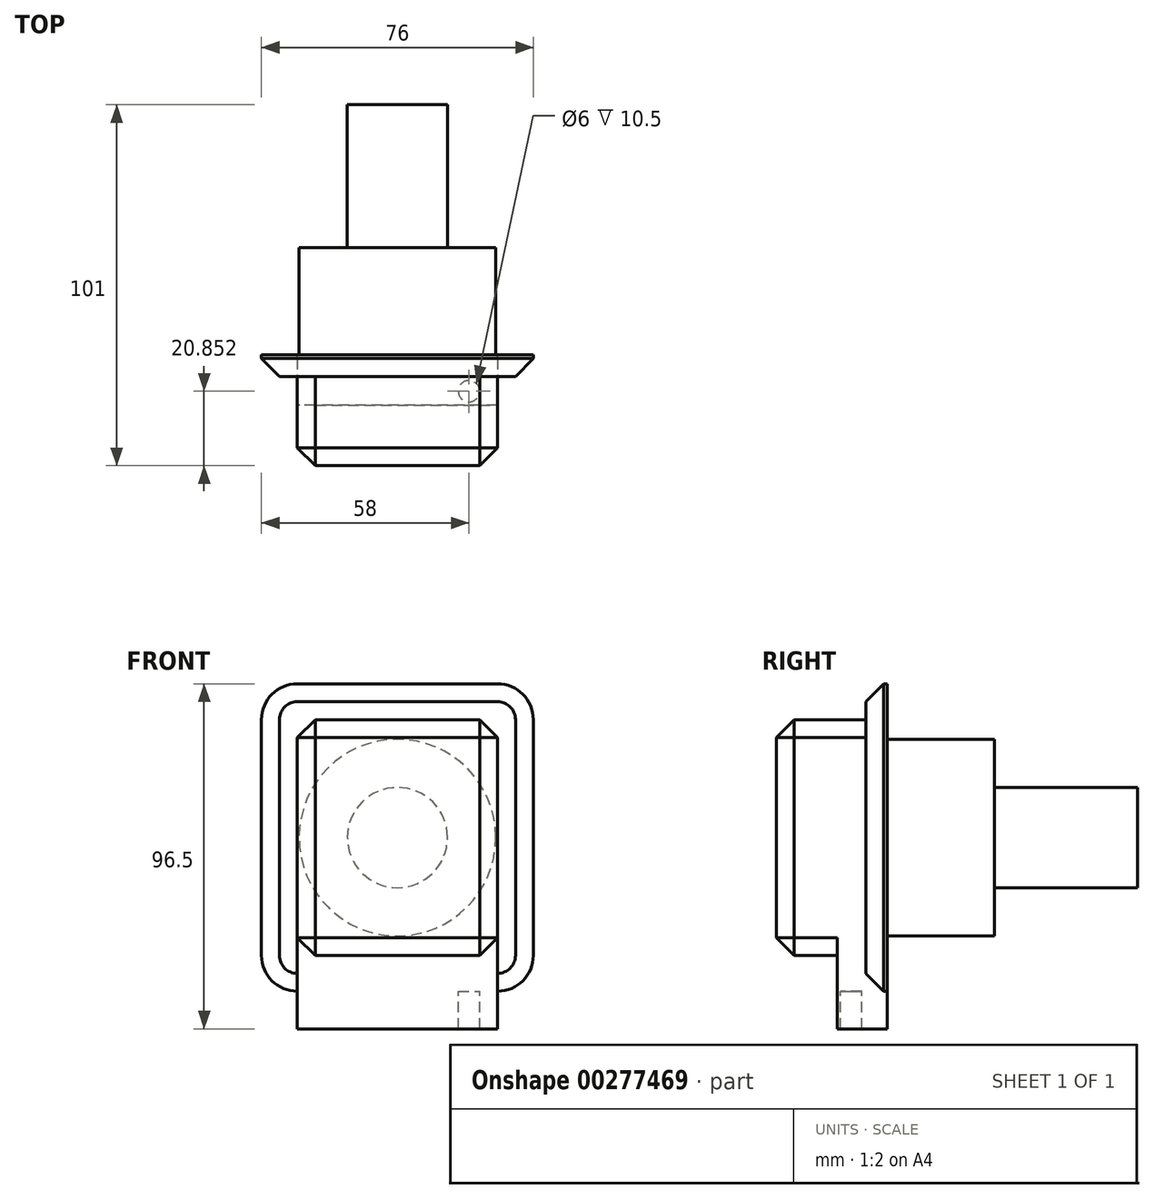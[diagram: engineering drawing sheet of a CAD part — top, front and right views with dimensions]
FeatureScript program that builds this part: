
annotation { "Feature Type Name" : "Feature", "Feature Type Description" : "" }
export const myFeature = defineFeature(function(context is Context, id is Id, definition is map)
    precondition{}
    {
        {
            var Q0;
            Q0=qCreatedBy(makeId("Front.planeOp"),FACE);
            var sketch = newSketch(context, id + "F0", { "sketchPlane" : qUnion([Q0])});
            skLineSegment(sketch, "E0.bottom", {"start": v(28, 43) * mm, "end": v(-28, 43) * mm});
            skLineSegment(sketch, "E0.top", {"start": v(28, -43) * mm, "end": v(-28, -43) * mm});
            skLineSegment(sketch, "E0.left", {"start": v(38, 33) * mm, "end": v(38, -33) * mm});
            skLineSegment(sketch, "E0.right", {"start": v(-38, 33) * mm, "end": v(-38, -33) * mm});
            skPoint(sketch, "E0.middle", {"position": v(0, 0) * mm});
            skPoint(sketch, "E1.visualSharp", {"position": v(-38, 43) * mm});
            skArc(sketch, "E1.filletArc", {"start": v(-28, 43) * mm, "mid": v(-35.07, 40.07) * mm, "end": v(-38, 33) * mm});
            skPoint(sketch, "E2.visualSharp", {"position": v(38, 43) * mm});
            skArc(sketch, "E2.filletArc", {"start": v(38, 33) * mm, "mid": v(35.07, 40.07) * mm, "end": v(28, 43) * mm});
            skPoint(sketch, "E3.visualSharp", {"position": v(38, -43) * mm});
            skArc(sketch, "E3.filletArc", {"start": v(28, -43) * mm, "mid": v(35.07, -40.07) * mm, "end": v(38, -33) * mm});
            skPoint(sketch, "E4.visualSharp", {"position": v(-38, -43) * mm});
            skArc(sketch, "E4.filletArc", {"start": v(-38, -33) * mm, "mid": v(-35.07, -40.07) * mm, "end": v(-28, -43) * mm});
            skSolve(sketch);
        }
        {
            var Q0;
            Q0=qSketchRegion(id+"F0",true);
            extrude(context, id + "F1", {"entities" : qUnion([Q0]), "depth" : 6 * mm});
        }
        {
            var Q0;
            Q0=makeQuery(id+"F1.opExtrude","CAP_FACE",FACE,{"disambiguationData":[OSD([sQuery(id+"F0.wireOp",EDGE,"E0.bottom"),sQuery(id+"F0.wireOp",EDGE,"E0.top"),sQuery(id+"F0.wireOp",EDGE,"E0.left"),sQuery(id+"F0.wireOp",EDGE,"E0.right")])],"isStart":true});
            var sketch = newSketch(context, id + "F2", { "sketchPlane" : qUnion([Q0])});
            skCircle(sketch, "E5", {"center": v(0, 0) * mm, "radius": 27.5 * mm});
            skSolve(sketch);
        }
        {
            var Q0;
            Q0=qSketchRegion(id+"F2",true);
            extrude(context, id + "F3", {"entities" : qUnion([Q0]), "operationType" : NewBodyOperationType.ADD, "depth" : 30 * mm});
        }
        {
            var Q0;
            Q0=makeQuery(id+"F3.opExtrude","CAP_FACE",FACE,{"disambiguationData":[OSD([sQuery(id+"F2.wireOp",EDGE,"E5")])],"isStart":false});
            var sketch = newSketch(context, id + "F4", { "sketchPlane" : qUnion([Q0])});
            skCircle(sketch, "E6", {"center": v(0, 0) * mm, "radius": 14 * mm});
            skSolve(sketch);
        }
        {
            var Q0;
            Q0=makeQuery(id+"F4.imprint","IMPRINT",FACE,{"disambiguationData":[TD([[makeQuery(id+"F4.imprint","IMPRINT",EDGE,{"derivedFrom":sQuery(id+"F4.wireOp",EDGE,"E6")}),1.0]])]});
            extrude(context, id + "F5", {"entities" : qUnion([Q0]), "operationType" : NewBodyOperationType.ADD, "depth" : 40 * mm});
        }
        {
            var Q0;
            Q0=makeQuery(id+"F1.opExtrude","CAP_FACE",FACE,{"disambiguationData":[OSD([sQuery(id+"F0.wireOp",EDGE,"E0.bottom"),sQuery(id+"F0.wireOp",EDGE,"E0.top"),sQuery(id+"F0.wireOp",EDGE,"E0.left"),sQuery(id+"F0.wireOp",EDGE,"E0.right"),sQuery(id+"F0.wireOp",EDGE,"E1.filletArc"),sQuery(id+"F0.wireOp",EDGE,"E2.filletArc"),sQuery(id+"F0.wireOp",EDGE,"E3.filletArc"),sQuery(id+"F0.wireOp",EDGE,"E4.filletArc")])],"isStart":false});
            var sketch = newSketch(context, id + "F6", { "sketchPlane" : qUnion([Q0])});
            skPoint(sketch, "E7.0", {"position": v(-28, -43) * mm});
            skLineSegment(sketch, "E8.bottom", {"start": v(-28, -43) * mm, "end": v(28, -43) * mm});
            skLineSegment(sketch, "E8.top", {"start": v(-28, -33) * mm, "end": v(28, -33) * mm});
            skLineSegment(sketch, "E8.left", {"start": v(-28, -43) * mm, "end": v(-28, -33) * mm});
            skLineSegment(sketch, "E8.right", {"start": v(28, -43) * mm, "end": v(28, -33) * mm});
            skSolve(sketch);
        }
        {
            var Q0;
            Q0=qSketchRegion(id+"F6",true);
            extrude(context, id + "F7", {"entities" : qUnion([Q0]), "operationType" : NewBodyOperationType.ADD, "depth" : 8 * mm});
        }
        {
            var Q0;
            Q0=makeQuery(id+"F7.boolean.opBoolean","MERGE",FACE,{"derivedFrom":[makeQuery(id+"F1.opExtrude","SWEPT_FACE",FACE,{"disambiguationData":[OSD([sQuery(id+"F0.wireOp",EDGE,"E0.top")])]}),makeQuery(id+"F7.opExtrude","SWEPT_FACE",FACE,{"disambiguationData":[OSD([sQuery(id+"F6.wireOp",EDGE,"E8.bottom")])]})]});
            var sketch = newSketch(context, id + "F8", { "sketchPlane" : qUnion([Q0])});
            skCircle(sketch, "E9", {"center": v(-20, 10.15) * mm, "radius": 3 * mm});
            skCircle(sketch, "E10.MirrorC", {"center": v(20, 10.15) * mm, "radius": 3 * mm});
            skSolve(sketch);
        }
        {
            var Q0;
            Q0=makeQuery(id+"F8.imprint","IMPRINT",FACE,{"disambiguationData":[TD([[makeQuery(id+"F8.imprint","IMPRINT",EDGE,{"derivedFrom":sQuery(id+"F8.wireOp",EDGE,"E9")}),1.0]])]});
            var Q1;
            Q1=makeQuery(id+"F8.imprint","IMPRINT",FACE,{"disambiguationData":[TD([[makeQuery(id+"F8.imprint","IMPRINT",EDGE,{"derivedFrom":sQuery(id+"F8.wireOp",EDGE,"E10.MirrorC")}),-1.0]])]});
            extrude(context, id + "F9", {"entities" : qUnion([Q0, Q1]), "operationType" : NewBodyOperationType.ADD, "depth" : 10.5 * mm});
        }
        {
            var Q0;
            Q0=makeQuery(id+"F1.opExtrude","CAP_FACE",FACE,{"disambiguationData":[OSD([sQuery(id+"F0.wireOp",EDGE,"E0.bottom"),sQuery(id+"F0.wireOp",EDGE,"E0.top"),sQuery(id+"F0.wireOp",EDGE,"E0.left"),sQuery(id+"F0.wireOp",EDGE,"E0.right"),sQuery(id+"F0.wireOp",EDGE,"E1.filletArc"),sQuery(id+"F0.wireOp",EDGE,"E2.filletArc"),sQuery(id+"F0.wireOp",EDGE,"E3.filletArc"),sQuery(id+"F0.wireOp",EDGE,"E4.filletArc")])],"isStart":false});
            var sketch = newSketch(context, id + "F10", { "sketchPlane" : qUnion([Q0])});
            skLineSegment(sketch, "E11.bottom", {"start": v(-28, 33) * mm, "end": v(28, 33) * mm});
            skLineSegment(sketch, "E11.top", {"start": v(-28, -33) * mm, "end": v(28, -33) * mm});
            skLineSegment(sketch, "E11.left", {"start": v(-28, 33) * mm, "end": v(-28, -33) * mm});
            skLineSegment(sketch, "E11.right", {"start": v(28, 33) * mm, "end": v(28, -33) * mm});
            skSolve(sketch);
        }
        {
            var Q0;
            Q0=qSketchRegion(id+"F10",true);
            extrude(context, id + "F11", {"entities" : qUnion([Q0]), "operationType" : NewBodyOperationType.ADD, "depth" : 25 * mm});
        }
        {
            var Q0;
            Q0=makeQuery(id+"F11.opExtrude","CAP_EDGE",EDGE,{"disambiguationData":[OSD([sQuery(id+"F10.wireOp",EDGE,"E11.bottom")])],"isStart":false});
            var Q1;
            Q1=makeQuery(id+"F11.opExtrude","CAP_EDGE",EDGE,{"disambiguationData":[OSD([sQuery(id+"F10.wireOp",EDGE,"E11.right")])],"isStart":false});
            var Q2;
            Q2=makeQuery(id+"F11.opExtrude","CAP_EDGE",EDGE,{"disambiguationData":[OSD([sQuery(id+"F10.wireOp",EDGE,"E11.left")])],"isStart":false});
            var Q3;
            Q3=makeQuery(id+"F11.opExtrude","SWEPT_EDGE",EDGE,{"disambiguationData":[OSD([sQuery(id+"F10.wireOp",EDGE,"E11.bottom"),sQuery(id+"F10.wireOp",EDGE,"E11.left")])]});
            var Q4;
            Q4=makeQuery(id+"F11.opExtrude","SWEPT_EDGE",EDGE,{"disambiguationData":[OSD([sQuery(id+"F10.wireOp",EDGE,"E11.bottom"),sQuery(id+"F10.wireOp",EDGE,"E11.right")])]});
            var Q5;
            Q5=makeQuery(id+"F11.opExtrude","SWEPT_EDGE",EDGE,{"disambiguationData":[OSD([sQuery(id+"F6.wireOp",EDGE,"E8.right"),sQuery(id+"F10.wireOp",EDGE,"E11.top"),sQuery(id+"F10.wireOp",EDGE,"E11.right")])]});
            var Q6;
            Q6=makeQuery(id+"F11.opExtrude","CAP_EDGE",EDGE,{"disambiguationData":[OSD([sQuery(id+"F10.wireOp",EDGE,"E11.top")])],"isStart":false});
            var Q7;
            Q7=makeQuery(id+"F11.opExtrude","SWEPT_EDGE",EDGE,{"disambiguationData":[OSD([sQuery(id+"F6.wireOp",EDGE,"E8.left"),sQuery(id+"F10.wireOp",EDGE,"E11.top"),sQuery(id+"F10.wireOp",EDGE,"E11.left")])]});
            var Q8;
            Q8=makeQuery(id+"F1.opExtrude","CAP_EDGE",EDGE,{"disambiguationData":[OSD([sQuery(id+"F0.wireOp",EDGE,"E0.bottom")])],"isStart":false});
            chamfer(context, id + "F12", {"entities" : qUnion([Q0, Q1, Q2, Q3, Q4, Q5, Q6, Q7, Q8]), "width" : 5 * mm, "tangentPropagation" : true});
        }
    });
